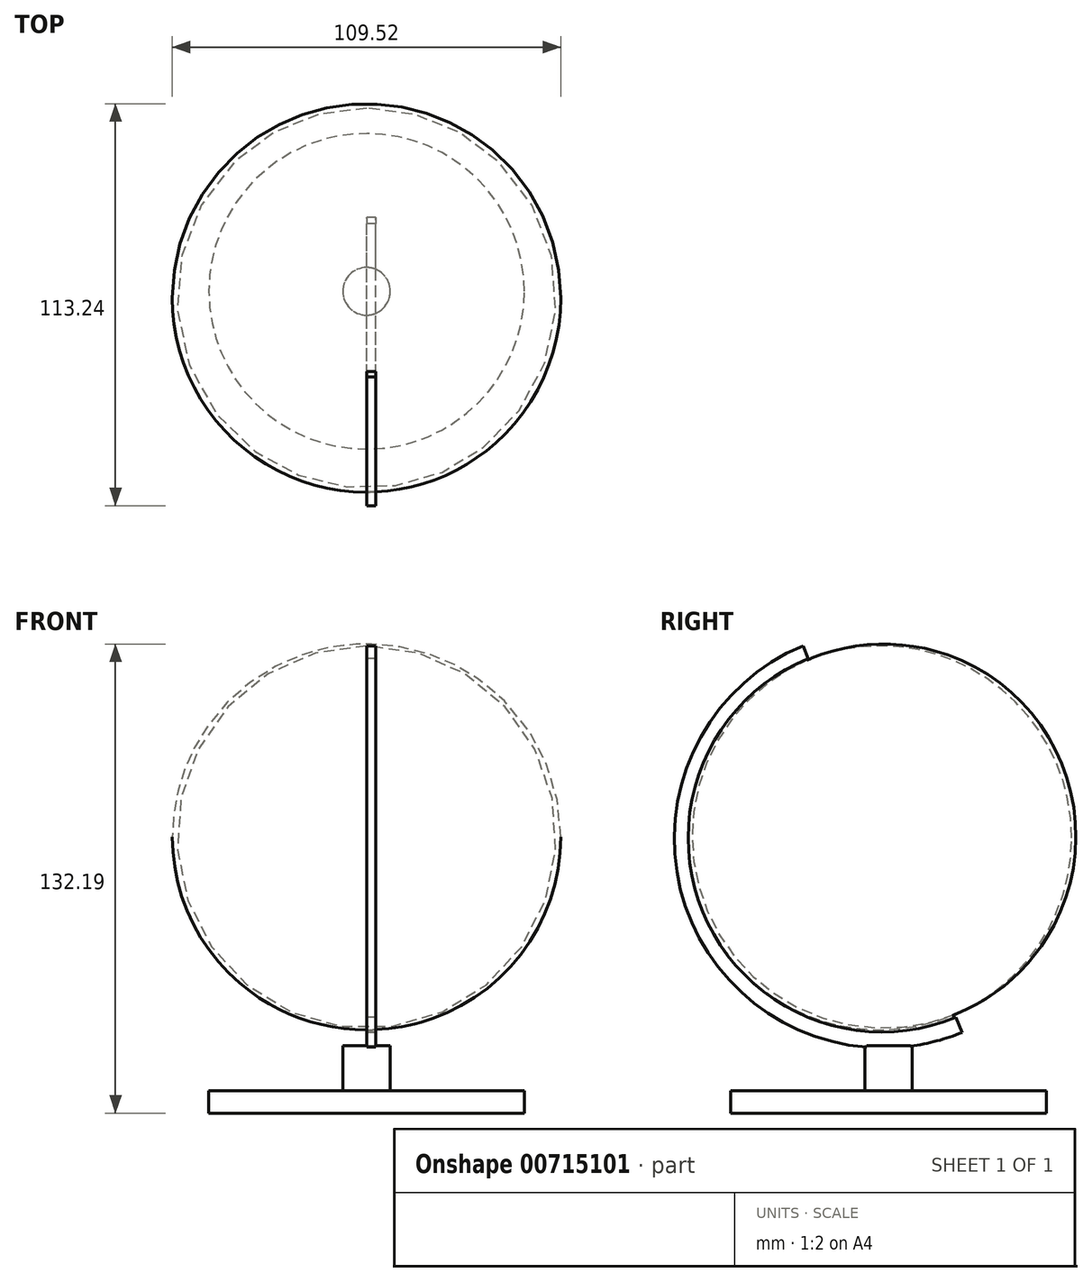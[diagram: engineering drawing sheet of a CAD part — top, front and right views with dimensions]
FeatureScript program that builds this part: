
annotation { "Feature Type Name" : "Feature", "Feature Type Description" : "" }
export const myFeature = defineFeature(function(context is Context, id is Id, definition is map)
    precondition{}
    {
        {
            var Q0;
            Q0=qCreatedBy(makeId("Top.planeOp"),FACE);
            var sketch = newSketch(context, id + "F0", { "sketchPlane" : qUnion([Q0])});
            skCircle(sketch, "E0", {"center": v(0, 0) * mm, "radius": 44.47 * mm});
            skSolve(sketch);
        }
        {
            var Q0;
            Q0 = qSketchRegion(id + "F0", true);
            extrude(context, id + "F1", {"entities" : qUnion([Q0]), "depth" : 6.35 * mm, "offsetDistance" : 25.4 * mm});
        }
        {
            var Q0;
            Q0=makeQuery(id+"F1.opExtrude","CAP_FACE",FACE,{"disambiguationData":[OSD([sQuery(id+"F0.wireOp",EDGE,"E0")])],"isStart":false});
            var sketch = newSketch(context, id + "F2", { "sketchPlane" : qUnion([Q0])});
            skCircle(sketch, "E1", {"center": v(0, 0) * mm, "radius": 6.7 * mm});
            skSolve(sketch);
        }
        {
            var Q0;
            Q0=makeQuery(id+"F2.imprint","IMPRINT",FACE,{"disambiguationData":[TD([[makeQuery(id+"F2.imprint","IMPRINT",EDGE,{"derivedFrom":sQuery(id+"F2.wireOp",EDGE,"E1")}),1.0]])]});
            extrude(context, id + "F3", {"entities" : qUnion([Q0]), "operationType" : NewBodyOperationType.ADD, "depth" : 12.7 * mm, "offsetDistance" : 25.4 * mm});
        }
        {
            var Q0;
            Q0=qCreatedBy(makeId("Right.planeOp"),FACE);
            var sketch = newSketch(context, id + "F4", { "sketchPlane" : qUnion([Q0])});
            skArc(sketch, "E2", {"start": v(-24.12, 131.7) * mm, "mid": v(-55.97, 54.85) * mm, "end": v(20.77, 22.73) * mm});
            skLineSegment(sketch, "E3", {"start": v(20.77, 22.73) * mm, "end": v(-24.12, 131.7) * mm});
            skLineSegment(sketch, "E4", {"start": v(-24.12, 131.7) * mm, "end": v(-22.64, 128.11) * mm});
            skLineSegment(sketch, "E5", {"start": v(20.77, 22.73) * mm, "end": v(19.01, 26.98) * mm});
            skArc(sketch, "E6", {"start": v(-22.64, 128.11) * mm, "mid": v(-52.38, 56.72) * mm, "end": v(19.01, 26.98) * mm});
            skSolve(sketch);
        }
        {
            var Q0;
            Q0=makeQuery(id+"F4.imprint","IMPRINT",FACE,{"disambiguationData":[TD([[makeQuery(id+"F4.imprint","IMPRINT",EDGE,{"derivedFrom":sQuery(id+"F4.wireOp",EDGE,"E2")}),1.0]])]});
            extrude(context, id + "F5", {"entities" : qUnion([Q0]), "operationType" : NewBodyOperationType.ADD, "depth" : 2.54 * mm, "offsetDistance" : 25.4 * mm});
        }
        {
            var Q0;
            Q0=qCreatedBy(makeId("Right.planeOp"),FACE);
            var sketch = newSketch(context, id + "F6", { "sketchPlane" : qUnion([Q0])});
            skArc(sketch, "E7", {"start": v(-22.33, 127.92) * mm, "mid": v(-51.36, 57.63) * mm, "end": v(18.57, 27.75) * mm});
            skLineSegment(sketch, "E8", {"start": v(-22.33, 127.92) * mm, "end": v(18.57, 27.75) * mm});
            skSolve(sketch);
        }
        {
            var Q0;
            Q0=makeQuery(id+"F6.imprint","IMPRINT",FACE,{"disambiguationData":[TD([[makeQuery(id+"F6.imprint","IMPRINT",EDGE,{"derivedFrom":sQuery(id+"F6.wireOp",EDGE,"E7")}),1.0]])]});
            var Q1;
            Q1=sQuery(id+"F6.wireOp",EDGE,"E8");
            revolve(context, id + "F7", {"surfaceOperationType" : NewSurfaceOperationType.NEW, "entities" : qUnion([Q0]), "axis" : qUnion([Q1]), "revolveType" : RevolveType.FULL});
        }
    });
